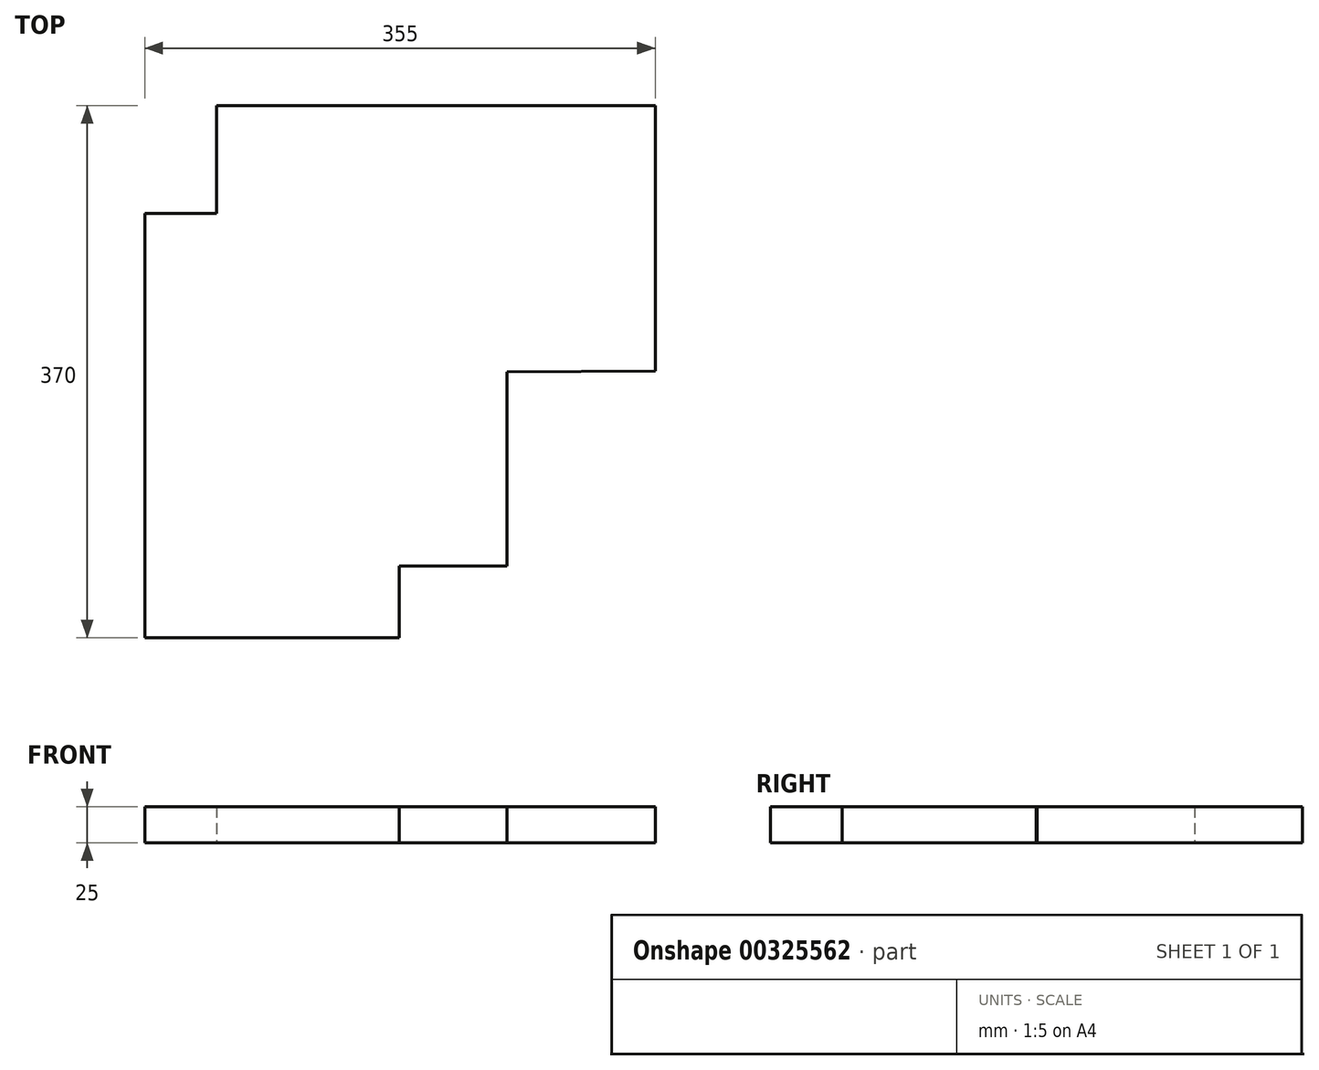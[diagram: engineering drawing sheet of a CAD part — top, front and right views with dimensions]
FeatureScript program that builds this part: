
annotation { "Feature Type Name" : "Feature", "Feature Type Description" : "" }
export const myFeature = defineFeature(function(context is Context, id is Id, definition is map)
    precondition{}
    {
        {
            var Q0;
            Q0=qCreatedBy(makeId("Top.planeOp"),FACE);
            var sketch = newSketch(context, id + "F0", { "sketchPlane" : qUnion([Q0])});
            skLineSegment(sketch, "E0", {"start": v(-169.85, -125.68) * mm, "end": v(7.15, -125.68) * mm});
            skLineSegment(sketch, "E1", {"start": v(7.15, -125.68) * mm, "end": v(7.15, -75.68) * mm});
            skLineSegment(sketch, "E2", {"start": v(7.15, -75.68) * mm, "end": v(82.15, -75.68) * mm});
            skLineSegment(sketch, "E3", {"start": v(-169.85, 169.32) * mm, "end": v(-169.85, -125.68) * mm});
            skLineSegment(sketch, "E4", {"start": v(-169.85, 169.32) * mm, "end": v(-119.85, 169.32) * mm});
            skLineSegment(sketch, "E5", {"start": v(-119.85, 169.32) * mm, "end": v(-119.85, 244.32) * mm});
            skLineSegment(sketch, "E6", {"start": v(-119.85, 244.32) * mm, "end": v(185.15, 244.32) * mm});
            skLineSegment(sketch, "E7", {"start": v(82.15, -75.68) * mm, "end": v(82.15, 59.32) * mm});
            skLineSegment(sketch, "E8", {"start": v(185.15, 244.32) * mm, "end": v(185.15, 59.69) * mm});
            skLineSegment(sketch, "E9", {"start": v(185.15, 59.69) * mm, "end": v(185.15, 59.69) * mm});
            skLineSegment(sketch, "E10", {"start": v(185.15, 59.69) * mm, "end": v(82.15, 59.32) * mm});
            skSolve(sketch);
        }
        {
            var Q0;
            Q0 = qSketchRegion(id + "F0", true);
            extrude(context, id + "F1", {"entities" : qUnion([Q0]), "depth" : 25 * mm});
        }
    });
